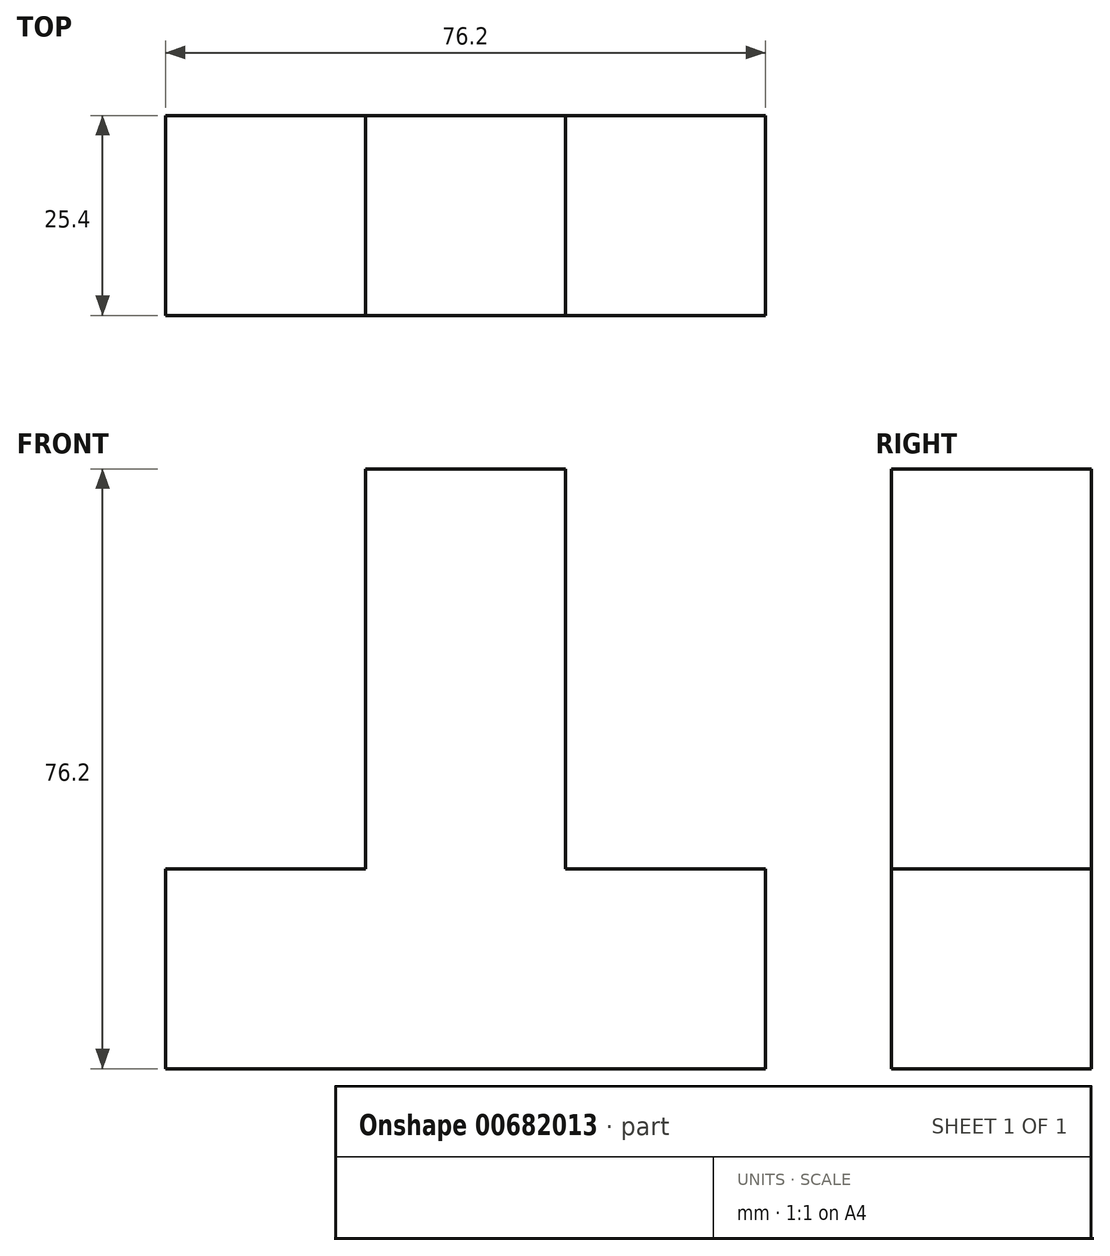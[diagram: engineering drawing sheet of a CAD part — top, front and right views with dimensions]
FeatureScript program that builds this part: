
annotation { "Feature Type Name" : "Feature", "Feature Type Description" : "" }
export const myFeature = defineFeature(function(context is Context, id is Id, definition is map)
    precondition{}
    {
        {
            var Q0;
            Q0=qCreatedBy(makeId("Front.planeOp"),FACE);
            var sketch = newSketch(context, id + "F0", { "sketchPlane" : qUnion([Q0])});
            skLineSegment(sketch, "E0", {"start": v(0, 0) * mm, "end": v(-76.2, 0) * mm});
            skLineSegment(sketch, "E1", {"start": v(-76.2, 0) * mm, "end": v(-76.2, 25.4) * mm});
            skLineSegment(sketch, "E2", {"start": v(-76.2, 25.4) * mm, "end": v(-50.8, 25.4) * mm});
            skLineSegment(sketch, "E3", {"start": v(-50.8, 25.4) * mm, "end": v(-50.8, 76.2) * mm});
            skLineSegment(sketch, "E4", {"start": v(-50.8, 76.2) * mm, "end": v(-25.4, 76.2) * mm});
            skLineSegment(sketch, "E5", {"start": v(-25.4, 76.2) * mm, "end": v(-25.4, 25.4) * mm});
            skLineSegment(sketch, "E6", {"start": v(-25.4, 25.4) * mm, "end": v(0, 25.4) * mm});
            skLineSegment(sketch, "E7", {"start": v(0, 25.4) * mm, "end": v(0, 0) * mm});
            skSolve(sketch);
        }
        {
            var Q0;
            Q0=makeQuery(id+"F0.imprint","IMPRINT",FACE,{"disambiguationData":[TD([[makeQuery(id+"F0.imprint","IMPRINT",EDGE,{"derivedFrom":sQuery(id+"F0.wireOp",EDGE,"E0")}),-1.0]])]});
            extrude(context, id + "F1", {"entities" : qUnion([Q0]), "depth" : 25.4 * mm, "offsetDistance" : 25.4 * mm});
        }
    });
